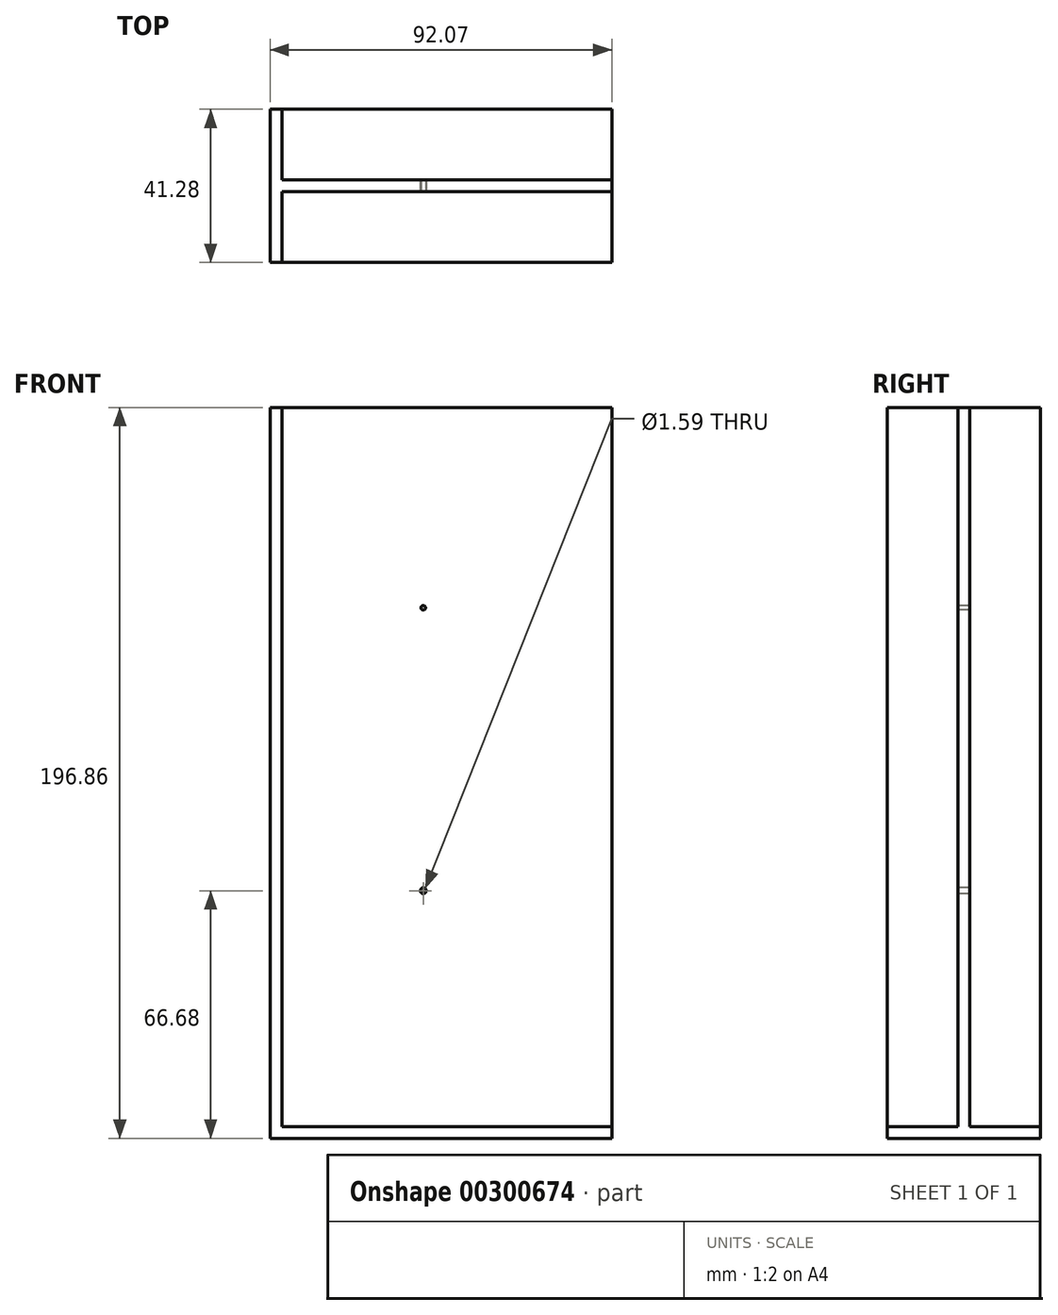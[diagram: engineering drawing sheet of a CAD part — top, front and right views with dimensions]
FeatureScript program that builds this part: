
annotation { "Feature Type Name" : "Feature", "Feature Type Description" : "" }
export const myFeature = defineFeature(function(context is Context, id is Id, definition is map)
    precondition{}
    {
        {
            var Q0;
            Q0=qCreatedBy(makeId("Top.planeOp"),FACE);
            var sketch = newSketch(context, id + "F0", { "sketchPlane" : qUnion([Q0])});
            skLineSegment(sketch, "E0", {"start": v(0, 20.64) * mm, "end": v(-3.18, 20.64) * mm});
            skLineSegment(sketch, "E1", {"start": v(-3.18, 20.64) * mm, "end": v(-3.17, -20.64) * mm});
            skLineSegment(sketch, "E2", {"start": v(-3.17, -20.64) * mm, "end": v(0, -20.64) * mm});
            skLineSegment(sketch, "E3", {"start": v(0, -20.64) * mm, "end": v(0, -1.59) * mm});
            skLineSegment(sketch, "E4", {"start": v(0, -1.59) * mm, "end": v(88.9, -1.59) * mm});
            skLineSegment(sketch, "E5", {"start": v(88.9, -1.59) * mm, "end": v(88.9, 1.59) * mm});
            skLineSegment(sketch, "E6", {"start": v(88.9, 1.59) * mm, "end": v(0, 1.59) * mm});
            skLineSegment(sketch, "E7", {"start": v(0, 1.59) * mm, "end": v(0, 20.64) * mm});
            skSolve(sketch);
        }
        {
            var Q0;
            Q0 = qSketchRegion(id + "F0", true);
            extrude(context, id + "F1", {"entities" : qUnion([Q0]), "depth" : 193.67 * mm});
        }
        {
            var Q0;
            Q0=makeQuery(id+"F1.opExtrude","CAP_FACE",FACE,{"disambiguationData":[OSD([sQuery(id+"F0.wireOp",EDGE,"E0"),sQuery(id+"F0.wireOp",EDGE,"E1"),sQuery(id+"F0.wireOp",EDGE,"E2"),sQuery(id+"F0.wireOp",EDGE,"E3"),sQuery(id+"F0.wireOp",EDGE,"E4"),sQuery(id+"F0.wireOp",EDGE,"E5"),sQuery(id+"F0.wireOp",EDGE,"E6"),sQuery(id+"F0.wireOp",EDGE,"E7")])],"isStart":true});
            var sketch = newSketch(context, id + "F2", { "sketchPlane" : qUnion([Q0])});
            skLineSegment(sketch, "E8.bottom", {"start": v(-3.18, -20.64) * mm, "end": v(88.9, -20.64) * mm});
            skLineSegment(sketch, "E8.top", {"start": v(-3.18, 20.64) * mm, "end": v(88.9, 20.64) * mm});
            skLineSegment(sketch, "E8.left", {"start": v(-3.18, -20.64) * mm, "end": v(-3.18, 20.64) * mm});
            skLineSegment(sketch, "E8.right", {"start": v(88.9, -20.64) * mm, "end": v(88.9, 20.64) * mm});
            skSolve(sketch);
        }
        {
            var Q0;
            Q0 = qSketchRegion(id + "F2", true);
            extrude(context, id + "F3", {"entities" : qUnion([Q0]), "operationType" : NewBodyOperationType.ADD, "depth" : 3.17 * mm});
        }
        {
            var Q0;
            Q0=makeQuery(id+"F1.opExtrude","SWEPT_FACE",FACE,{"disambiguationData":[OSD([sQuery(id+"F0.wireOp",EDGE,"E4")])]});
            var sketch = newSketch(context, id + "F4", { "sketchPlane" : qUnion([Q0])});
            skCircle(sketch, "E9", {"center": v(38.1, 63.5) * mm, "radius": 0.8 * mm});
            skCircle(sketch, "E10", {"center": v(38.1, 139.7) * mm, "radius": 0.62 * mm});
            skSolve(sketch);
        }
        {
            var Q0;
            Q0 = qSketchRegion(id + "F4", true);
            extrude(context, id + "F5", {"entities" : qUnion([Q0]), "operationType" : NewBodyOperationType.REMOVE, "endBound" : BoundingType.UP_TO_NEXT, "oppositeDirection" : true, "depth" : 25.4 * mm});
        }
    });
